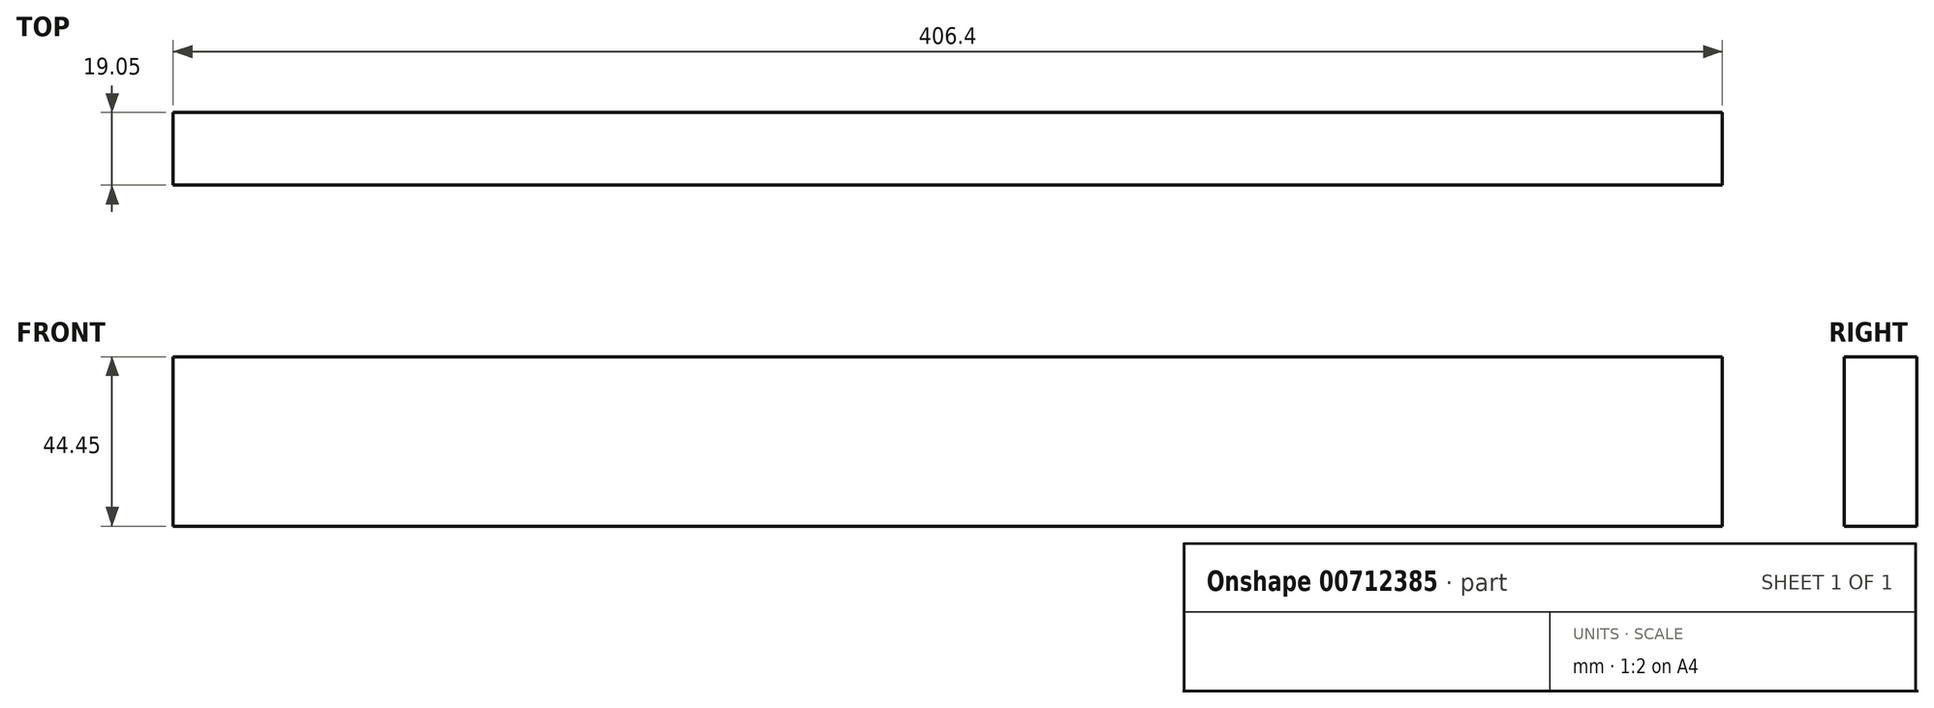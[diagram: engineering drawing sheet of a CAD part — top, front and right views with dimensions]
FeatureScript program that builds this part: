
annotation { "Feature Type Name" : "Feature", "Feature Type Description" : "" }
export const myFeature = defineFeature(function(context is Context, id is Id, definition is map)
    precondition{}
    {
        {
            var Q0;
            Q0=qCreatedBy(makeId("Front.planeOp"),FACE);
            var sketch = newSketch(context, id + "F0", { "sketchPlane" : qUnion([Q0])});
            skLineSegment(sketch, "E0.bottom", {"start": v(0, 0) * mm, "end": v(406.4, 0) * mm});
            skLineSegment(sketch, "E0.top", {"start": v(0, 44.45) * mm, "end": v(406.4, 44.45) * mm});
            skLineSegment(sketch, "E0.left", {"start": v(0, 0) * mm, "end": v(0, 44.45) * mm});
            skLineSegment(sketch, "E0.right", {"start": v(406.4, 0) * mm, "end": v(406.4, 44.45) * mm});
            skSolve(sketch);
        }
        {
            var Q0;
            Q0=makeQuery(id+"F0.imprint","IMPRINT",FACE,{"disambiguationData":[TD([[makeQuery(id+"F0.imprint","IMPRINT",EDGE,{"derivedFrom":sQuery(id+"F0.wireOp",EDGE,"E0.bottom")}),1.0]])]});
            extrude(context, id + "F1", {"entities" : qUnion([Q0]), "depth" : 19.05 * mm, "offsetDistance" : 25.4 * mm});
        }
    });
